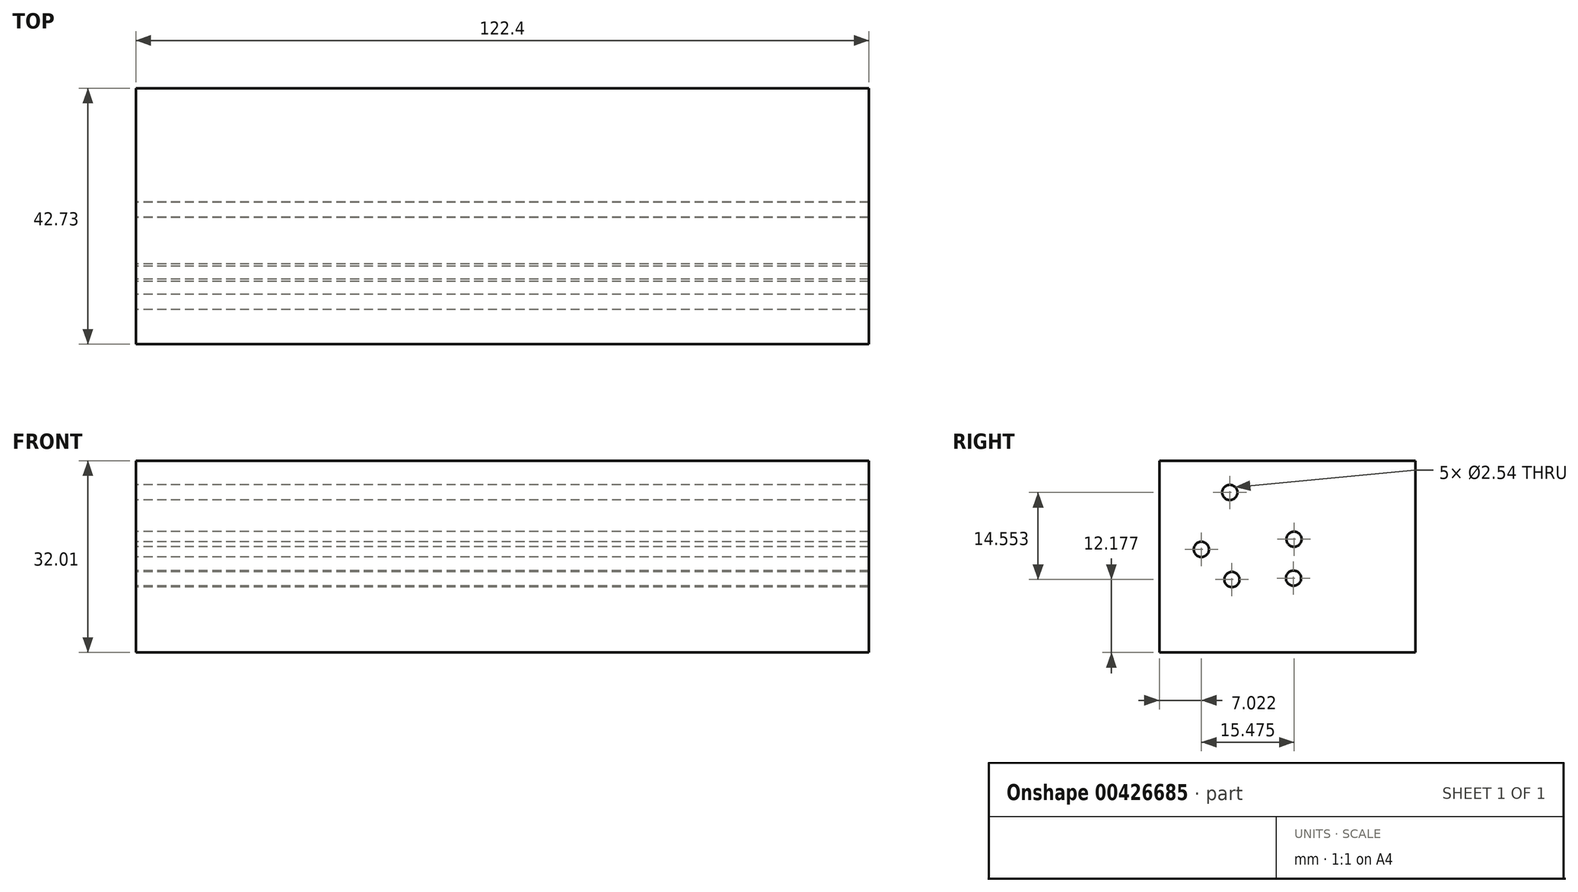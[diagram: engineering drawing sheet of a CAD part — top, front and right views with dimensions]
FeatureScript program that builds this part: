
annotation { "Feature Type Name" : "Feature", "Feature Type Description" : "" }
export const myFeature = defineFeature(function(context is Context, id is Id, definition is map)
    precondition{}
    {
        {
            var Q0;
            Q0=qCreatedBy(makeId("Top.planeOp"),FACE);
            var sketch = newSketch(context, id + "F0", { "sketchPlane" : qUnion([Q0])});
            skLineSegment(sketch, "E0.bottom", {"start": v(-62.65, 59.33) * mm, "end": v(59.75, 59.33) * mm});
            skLineSegment(sketch, "E0.top", {"start": v(-62.65, 16.6) * mm, "end": v(59.75, 16.6) * mm});
            skLineSegment(sketch, "E0.left", {"start": v(-62.65, 59.33) * mm, "end": v(-62.65, 16.6) * mm});
            skLineSegment(sketch, "E0.right", {"start": v(59.75, 59.33) * mm, "end": v(59.75, 16.6) * mm});
            skSolve(sketch);
        }
        {
            var Q0;
            Q0=makeQuery(id+"F0.imprint","IMPRINT",FACE,{"disambiguationData":[TD([[makeQuery(id+"F0.imprint","IMPRINT",EDGE,{"derivedFrom":sQuery(id+"F0.wireOp",EDGE,"E0.bottom")}),-1.0]])]});
            extrude(context, id + "F1", {"entities" : qUnion([Q0]), "depth" : 32 * mm});
        }
        {
            var Q0;
            Q0=makeQuery(id+"F1.opExtrude","SWEPT_FACE",FACE,{"disambiguationData":[OSD([sQuery(id+"F0.wireOp",EDGE,"E0.left")])]});
            var sketch = newSketch(context, id + "F2", { "sketchPlane" : qUnion([Q0])});
            skCircle(sketch, "E1", {"center": v(-37.96, 19.92) * mm, "radius": 8.14 * mm});
            skPoint(sketch, "E1.centerSnap0", {"position": v(-37.96, 32) * mm});
            skCircle(sketch, "E2.1.0", {"center": v(1.73, -42.84) * mm, "radius": 8.14 * mm});
            skCircle(sketch, "E2.2.0", {"center": v(36.23, 22.92) * mm, "radius": 8.14 * mm});
            skPoint(sketch, "E2.center", {"position": v(0, 0) * mm});
            skLineSegment(sketch, "E2.anchor1", {"start": v(0, 0) * mm, "end": v(-37.96, 19.92) * mm, "construction": true});
            skLineSegment(sketch, "E2.anchor2", {"start": v(0, 0) * mm, "end": v(36.23, 22.92) * mm, "construction": true});
            skSolve(sketch);
        }
        {
            var Q0;
            Q0=sQuery(id+"F2.wireOp",EDGE,"E1");
            extrude(context, id + "F3", {"bodyType" : ToolBodyType.SURFACE, "surfaceEntities" : qUnion([Q0]), "depth" : 25.4 * mm, "hasSecondDirection" : true, "secondDirectionOppositeDirection" : true, "secondDirectionDepth" : 189.8 * mm});
        }
        {
            var Q0;
            Q0=makeQuery(id+"F1.opExtrude","SWEPT_FACE",FACE,{"disambiguationData":[OSD([sQuery(id+"F0.wireOp",EDGE,"E0.left")])]});
            var sketch = newSketch(context, id + "F4", { "sketchPlane" : qUnion([Q0])});
            skPoint(sketch, "E3", {"position": v(-39.1, 18.91) * mm});
            skPoint(sketch, "E4", {"position": v(-23.62, 17.21) * mm});
            skPoint(sketch, "E5", {"position": v(-28.72, 12.18) * mm});
            skPoint(sketch, "E6", {"position": v(-39, 12.4) * mm});
            skPoint(sketch, "E7", {"position": v(-28.37, 26.73) * mm});
            skSolve(sketch);
        }
        {
            var Q0;
            Q0=sQuery(id+"F4.wireOp",VERTEX,"E7");
            var Q1;
            Q1=sQuery(id+"F4.wireOp",VERTEX,"E4");
            var Q2;
            Q2=sQuery(id+"F4.wireOp",VERTEX,"E5");
            var Q3;
            Q3=sQuery(id+"F4.wireOp",VERTEX,"E6");
            var Q4;
            Q4=sQuery(id+"F4.wireOp",VERTEX,"E3");
            var Q5;
            Q5=makeQuery(id+"F1.opExtrude","SWEPT_BODY",BODY,{"disambiguationData":[OSD([sQuery(id+"F0.wireOp",EDGE,"E0.bottom"),sQuery(id+"F0.wireOp",EDGE,"E0.top"),sQuery(id+"F0.wireOp",EDGE,"E0.left"),sQuery(id+"F0.wireOp",EDGE,"E0.right")])]});
            hole(context, id + "F5", {"style" : HoleStyle.SIMPLE, "endStyle" : HoleEndStyle.THROUGH, "holeDiameter" : 2.54 * mm, "isTappedThrough" : true, "tappedDepth" : 12.7 * mm, "tapClearance" : 3, "locations" : qUnion([Q0, Q1, Q2, Q3, Q4]), "scope" : qUnion([Q5])});
        }
    });
